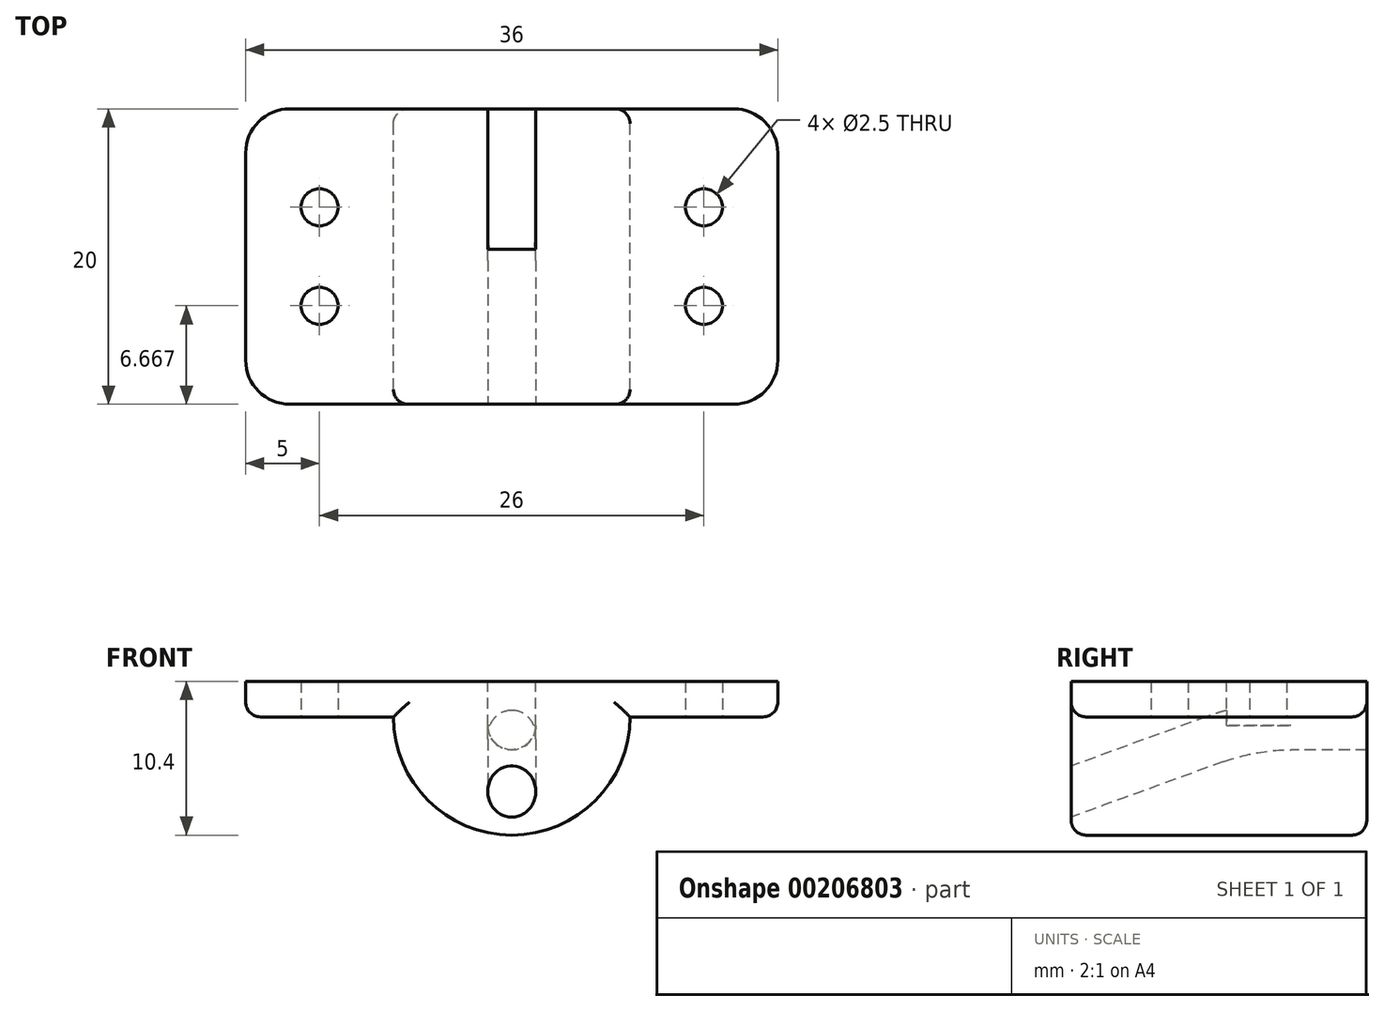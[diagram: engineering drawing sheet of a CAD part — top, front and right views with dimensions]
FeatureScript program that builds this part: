
annotation { "Feature Type Name" : "Feature", "Feature Type Description" : "" }
export const myFeature = defineFeature(function(context is Context, id is Id, definition is map)
    precondition{}
    {
        {
            var Q0;
            Q0=qCreatedBy(makeId("Top.planeOp"),FACE);
            var sketch = newSketch(context, id + "F0", { "sketchPlane" : qUnion([Q0])});
            skLineSegment(sketch, "E0", {"start": v(-38, 0) * mm, "end": v(0, 0) * mm, "construction": true});
            skSolve(sketch);
        }
        {
            var Q0;
            Q0=qCreatedBy(makeId("Front.planeOp"),FACE);
            var sketch = newSketch(context, id + "F1", { "sketchPlane" : qUnion([Q0])});
            skLineSegment(sketch, "E1", {"start": v(0, 0) * mm, "end": v(-18, 0) * mm});
            skLineSegment(sketch, "E2", {"start": v(-18, 0) * mm, "end": v(-18, -2.4) * mm});
            skLineSegment(sketch, "E3", {"start": v(-18, -2.4) * mm, "end": v(-8, -2.4) * mm});
            skArc(sketch, "E4.0", {"start": v(-8, -2.4) * mm, "mid": v(0, -10.4) * mm, "end": v(8, -2.4) * mm});
            skLineSegment(sketch, "E5.MirrorCS", {"start": v(0, 0) * mm, "end": v(18, 0) * mm});
            skLineSegment(sketch, "E6.MirrorCS", {"start": v(18, -2.4) * mm, "end": v(8, -2.4) * mm});
            skLineSegment(sketch, "E7.MirrorCS", {"start": v(18, 0) * mm, "end": v(18, -2.4) * mm});
            skSolve(sketch);
        }
        {
            var Q0;
            Q0 = qSketchRegion(id + "F1", true);
            extrude(context, id + "F2", {"entities" : qUnion([Q0]), "depth" : 20 * mm});
        }
        {
            var Q0;
            Q0=qCreatedBy(makeId("Right.planeOp"),FACE);
            var sketch = newSketch(context, id + "F3", { "sketchPlane" : qUnion([Q0])});
            skLineSegment(sketch, "E8", {"start": v(-24.86, -9.22) * mm, "end": v(-10.26, -3.9) * mm});
            skArc(sketch, "E9", {"start": v(-5.13, -3) * mm, "mid": v(-7.74, -3.23) * mm, "end": v(-10.26, -3.9) * mm});
            skLineSegment(sketch, "E10", {"start": v(0, 0) * mm, "end": v(0, -13.95) * mm, "construction": true});
            skLineSegment(sketch, "E11", {"start": v(-5.13, -3) * mm, "end": v(0, -3) * mm});
            skPoint(sketch, "E12.orphan", {"position": v(0, -3.9) * mm});
            skSolve(sketch);
        }
        {
            var Q0;
            Q0=makeQuery(id+"F2.opExtrude","CAP_FACE",FACE,{"disambiguationData":[OSD([sQuery(id+"F1.wireOp",EDGE,"E1"),sQuery(id+"F1.wireOp",EDGE,"E2"),sQuery(id+"F1.wireOp",EDGE,"E3"),sQuery(id+"F1.wireOp",EDGE,"E4.0"),sQuery(id+"F1.wireOp",EDGE,"E5.MirrorCS"),sQuery(id+"F1.wireOp",EDGE,"E6.MirrorCS"),sQuery(id+"F1.wireOp",EDGE,"E7.MirrorCS")])],"isStart":true});
            var sketch = newSketch(context, id + "F4", { "sketchPlane" : qUnion([Q0])});
            skCircle(sketch, "E13", {"center": v(0, -3) * mm, "radius": 1.63 * mm});
            skSolve(sketch);
        }
        {
            var Q0;
            Q0=makeQuery(id+"F4.imprint","IMPRINT",FACE,{"disambiguationData":[TD([[makeQuery(id+"F4.imprint","IMPRINT",EDGE,{"derivedFrom":sQuery(id+"F4.wireOp",EDGE,"E13")}),1.0]])]});
            var Q1;
            Q1=sQuery(id+"F4.wireOp",EDGE,"E13");
            var Q2;
            Q2=sQuery(id+"F3.wireOp",EDGE,"E11");
            var Q3;
            Q3=sQuery(id+"F3.wireOp",EDGE,"E9");
            var Q4;
            Q4=sQuery(id+"F3.wireOp",EDGE,"E8");
            var Q5;
            Q5=sQuery(id+"F3.wireOp",EDGE,"E11");
            var Q6;
            Q6=sQuery(id+"F3.wireOp",EDGE,"E9");
            var Q7;
            Q7=sQuery(id+"F3.wireOp",EDGE,"E8");
            sweep(context, id + "F5", {"operationType" : NewBodyOperationType.REMOVE, "profiles" : qUnion([Q0]), "surfaceProfiles" : qUnion([Q1, Q2, Q3, Q4]), "path" : qUnion([Q5, Q6, Q7])});
        }
        {
            var Q0;
            Q0=makeQuery(id+"F2.opExtrude","SWEPT_FACE",FACE,{"disambiguationData":[OSD([sQuery(id+"F1.wireOp",EDGE,"E1"),sQuery(id+"F1.wireOp",EDGE,"E5.MirrorCS")])]});
            var sketch = newSketch(context, id + "F6", { "sketchPlane" : qUnion([Q0])});
            skLineSegment(sketch, "E14.0", {"start": v(0, -5.13) * mm, "end": v(0, 0) * mm, "construction": true});
            skLineSegment(sketch, "E15.0", {"start": v(0, -5.13) * mm, "end": v(0, -10.26) * mm, "construction": true});
            skLineSegment(sketch, "E16.0", {"start": v(0, -24.86) * mm, "end": v(0, -10.26) * mm, "construction": true});
            skLineSegment(sketch, "E17.0", {"start": v(1.63, -5.13) * mm, "end": v(1.63, 0) * mm});
            skLineSegment(sketch, "E18.0", {"start": v(1.63, -5.13) * mm, "end": v(1.63, -9.5) * mm});
            skLineSegment(sketch, "E19.MirrorCS", {"start": v(-1.63, -5.13) * mm, "end": v(-1.63, 0) * mm});
            skLineSegment(sketch, "E20.MirrorCS", {"start": v(-1.63, -5.13) * mm, "end": v(-1.62, -9.5) * mm});
            skLineSegment(sketch, "E21", {"start": v(1.63, 0) * mm, "end": v(-1.63, 0) * mm});
            skLineSegment(sketch, "E22", {"start": v(1.63, -9.5) * mm, "end": v(-1.63, -9.5) * mm});
            skLineSegment(sketch, "E23.0", {"start": v(-38, 0) * mm, "end": v(0, 0) * mm, "construction": true});
            skSolve(sketch);
        }
        {
            var Q0;
            Q0 = qSketchRegion(id + "F6", true);
            var Q1;
            Q1=makeQuery(id+"F5.boolean.opBoolean","COPY",FACE,{"derivedFrom":makeQuery(id+"F5.opSweep","SWEPT_FACE",FACE,{"disambiguationData":[OSD([sQuery(id+"F3.wireOp",EDGE,"E9"),sQuery(id+"F4.wireOp",EDGE,"E13")])]})});
            extrude(context, id + "F7", {"entities" : qUnion([Q0]), "operationType" : NewBodyOperationType.REMOVE, "oppositeDirection" : true, "endBoundEntityFace" : qUnion([Q1]), "depth" : 3 * mm});
        }
        {
            var Q0;
            Q0=makeQuery(id+"F2.opExtrude","SWEPT_FACE",FACE,{"disambiguationData":[OSD([sQuery(id+"F1.wireOp",EDGE,"E6.MirrorCS")])]});
            var sketch = newSketch(context, id + "F8", { "sketchPlane" : qUnion([Q0])});
            skLineSegment(sketch, "E24", {"start": v(13, 20) * mm, "end": v(13, 13.33) * mm, "construction": true});
            skLineSegment(sketch, "E25", {"start": v(13, 13.33) * mm, "end": v(13, 6.67) * mm, "construction": true});
            skLineSegment(sketch, "E26", {"start": v(13, 6.67) * mm, "end": v(13, 0) * mm, "construction": true});
            skCircle(sketch, "E27", {"center": v(13, 13.33) * mm, "radius": 1.25 * mm});
            skCircle(sketch, "E28", {"center": v(13, 6.67) * mm, "radius": 1.25 * mm});
            skCircle(sketch, "E29.MirrorC", {"center": v(-13, 13.33) * mm, "radius": 1.25 * mm});
            skCircle(sketch, "E30.MirrorC", {"center": v(-13, 6.67) * mm, "radius": 1.25 * mm});
            skSolve(sketch);
        }
        {
            var Q0;
            Q0 = qSketchRegion(id + "F8", true);
            extrude(context, id + "F9", {"entities" : qUnion([Q0]), "operationType" : NewBodyOperationType.REMOVE, "endBound" : BoundingType.THROUGH_ALL, "oppositeDirection" : true, "depth" : 25 * mm});
        }
        {
            var Q0;
            Q0=makeQuery(id+"F2.opExtrude","CAP_EDGE",EDGE,{"disambiguationData":[OSD([sQuery(id+"F1.wireOp",EDGE,"E7.MirrorCS")])],"isStart":false});
            var Q1;
            Q1=makeQuery(id+"F2.opExtrude","CAP_EDGE",EDGE,{"disambiguationData":[OSD([sQuery(id+"F1.wireOp",EDGE,"E7.MirrorCS")])],"isStart":true});
            var Q2;
            Q2=makeQuery(id+"F2.opExtrude","CAP_EDGE",EDGE,{"disambiguationData":[OSD([sQuery(id+"F1.wireOp",EDGE,"E2")])],"isStart":false});
            var Q3;
            Q3=makeQuery(id+"F2.opExtrude","CAP_EDGE",EDGE,{"disambiguationData":[OSD([sQuery(id+"F1.wireOp",EDGE,"E2")])],"isStart":true});
            fillet(context, id + "F10", {"entities" : qUnion([Q0, Q1, Q2, Q3]), "radius" : 3 * mm, "tangentPropagation" : true, "allowEdgeOverflow" : false});
        }
        {
            var Q0;
            Q0=makeQuery(id+"F2.opExtrude","CAP_EDGE",EDGE,{"disambiguationData":[OSD([sQuery(id+"F1.wireOp",EDGE,"E4.0")])],"isStart":false});
            var Q1;
            Q1=makeQuery(id+"F2.opExtrude","CAP_EDGE",EDGE,{"disambiguationData":[OSD([sQuery(id+"F1.wireOp",EDGE,"E3")])],"isStart":false});
            var Q2;
            Q2=makeQuery(id+"F2.opExtrude","CAP_EDGE",EDGE,{"disambiguationData":[OSD([sQuery(id+"F1.wireOp",EDGE,"E6.MirrorCS")])],"isStart":false});
            var Q3;
            Q3=makeQuery(id+"F2.opExtrude","CAP_EDGE",EDGE,{"disambiguationData":[OSD([sQuery(id+"F1.wireOp",EDGE,"E4.0")])],"isStart":true});
            fillet(context, id + "F11", {"entities" : qUnion([Q0, Q1, Q2, Q3]), "radius" : 1 * mm, "tangentPropagation" : true, "allowEdgeOverflow" : false});
        }
    });
